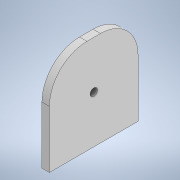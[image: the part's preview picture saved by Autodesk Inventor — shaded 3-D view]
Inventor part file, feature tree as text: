
AUTODESK INVENTOR PART (.ipt)
format: ipt  version: 2022 (Build 260153000, 153)  size: 114,688 bytes
history: native  units: mm
features: extrude x3, sketch x3, fillet x1
ambient origin geometry x8: Origin, YZ Plane, XZ Plane, XY Plane, X Axis, Y Axis, Z Axis, Center Point
bodies: Solid1 (feature_tree)
feature tree (7):
  extrude  "Extrusion1"  Depth=94.996mm
  extrude  "Extrusion2"  Depth=4.0mm
  extrude  "Extrusion3"  Depth=8.0mm
  fillet  "Fillet1"  [1 undecoded]
  sketch  "Sketch1"  dims[d0=101.6mm d1=94.996mm]
  sketch  "Sketch2"  dims[d2=8.0mm d3=0.0mm d6=4.0mm]
  sketch  "Sketch3"  dims[d7=8.0mm d8=0.0mm d9=8.0mm d10=0.0mm d11=0.0mm d12=40.25mm]
note: 1 required parameter value undecoded (feature->parameter linkage not recoverable at this tier; creation-order binding heuristic only, values carry confidence <= 0.55)
